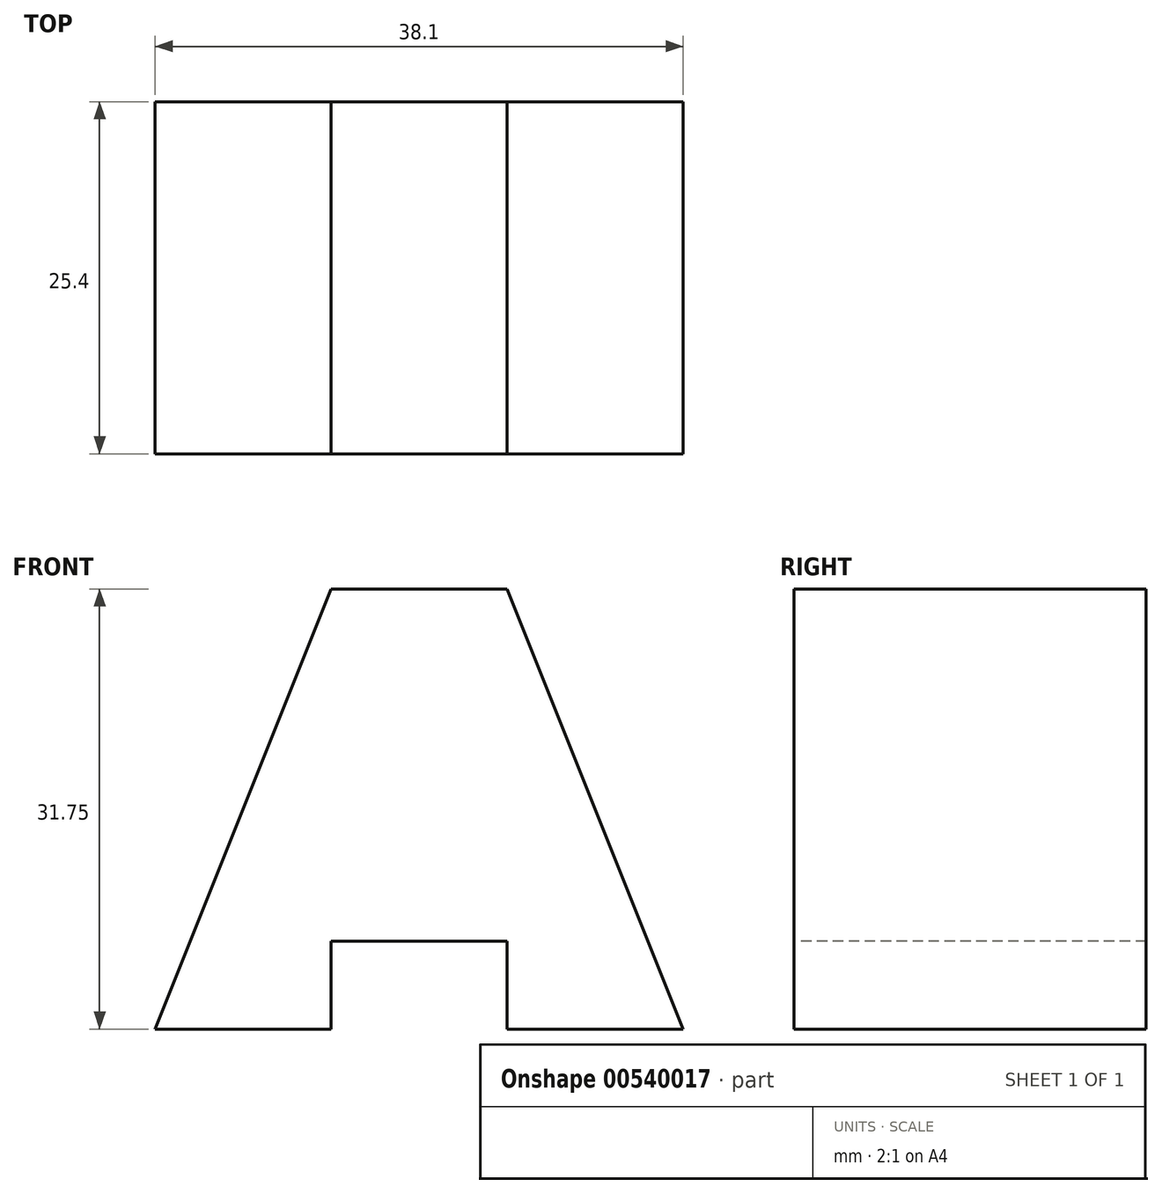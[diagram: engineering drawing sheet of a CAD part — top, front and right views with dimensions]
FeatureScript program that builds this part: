
annotation { "Feature Type Name" : "Feature", "Feature Type Description" : "" }
export const myFeature = defineFeature(function(context is Context, id is Id, definition is map)
    precondition{}
    {
        {
            var Q0;
            Q0=qCreatedBy(makeId("Front.planeOp"),FACE);
            var sketch = newSketch(context, id + "F0", { "sketchPlane" : qUnion([Q0])});
            skLineSegment(sketch, "E0", {"start": v(-62.77, 56) * mm, "end": v(-24.67, 56) * mm});
            skLineSegment(sketch, "E1", {"start": v(-24.67, 56) * mm, "end": v(-24.67, 24.26) * mm});
            skLineSegment(sketch, "E2", {"start": v(-24.67, 24.26) * mm, "end": v(-62.77, 24.26) * mm});
            skLineSegment(sketch, "E3", {"start": v(-62.77, 24.26) * mm, "end": v(-62.77, 56) * mm});
            skSolve(sketch);
        }
        {
            var Q0;
            Q0=makeQuery(id+"F0.imprint","IMPRINT",FACE,{"disambiguationData":[TD([[makeQuery(id+"F0.imprint","IMPRINT",EDGE,{"derivedFrom":sQuery(id+"F0.wireOp",EDGE,"E0")}),-1.0]])]});
            extrude(context, id + "F1", {"entities" : qUnion([Q0]), "depth" : 25.4 * mm, "offsetDistance" : 25.4 * mm});
        }
        {
            var Q0;
            Q0=makeQuery(id+"F1.opExtrude","CAP_FACE",FACE,{"disambiguationData":[OSD([sQuery(id+"F0.wireOp",EDGE,"E0"),sQuery(id+"F0.wireOp",EDGE,"E1"),sQuery(id+"F0.wireOp",EDGE,"E2"),sQuery(id+"F0.wireOp",EDGE,"E3")])],"isStart":false});
            var sketch = newSketch(context, id + "F2", { "sketchPlane" : qUnion([Q0])});
            skLineSegment(sketch, "E4", {"start": v(-50.07, 56) * mm, "end": v(-62.77, 24.26) * mm});
            skLineSegment(sketch, "E5", {"start": v(-37.37, 56) * mm, "end": v(-24.67, 24.26) * mm});
            skSolve(sketch);
        }
        {
            var Q0;
            {var subQ0=sQuery(id+"F2.wireOp",EDGE,"E4");Q0=makeQuery(id+"F2.imprint","IMPRINT",FACE,{"disambiguationData":[TD([[makeQuery(id+"F2.imprint","IMPRINT",EDGE,{"derivedFrom":subQ0}),-1.0]])]});}
            extrude(context, id + "F3", {"entities" : qUnion([Q0]), "operationType" : NewBodyOperationType.REMOVE, "oppositeDirection" : true, "depth" : 25.4 * mm, "offsetDistance" : 25.4 * mm});
        }
        {
            var Q0;
            Q0=makeQuery(id+"F1.opExtrude","CAP_FACE",FACE,{"disambiguationData":[OSD([sQuery(id+"F0.wireOp",EDGE,"E0"),sQuery(id+"F0.wireOp",EDGE,"E1"),sQuery(id+"F0.wireOp",EDGE,"E2"),sQuery(id+"F0.wireOp",EDGE,"E3")])],"isStart":false});
            var sketch = newSketch(context, id + "F4", { "sketchPlane" : qUnion([Q0])});
            skLineSegment(sketch, "E6", {"start": v(-37.37, 56) * mm, "end": v(-24.67, 24.26) * mm});
            skSolve(sketch);
        }
        {
            var Q0;
            {var subQ0=sQuery(id+"F4.wireOp",EDGE,"E6");Q0=makeQuery(id+"F4.imprint","IMPRINT",FACE,{"disambiguationData":[TD([[makeQuery(id+"F4.imprint","IMPRINT",EDGE,{"derivedFrom":subQ0}),1.0]])]});}
            extrude(context, id + "F5", {"entities" : qUnion([Q0]), "operationType" : NewBodyOperationType.REMOVE, "oppositeDirection" : true, "depth" : 25.4 * mm, "offsetDistance" : 25.4 * mm});
        }
        {
            var Q0;
            Q0=makeQuery(id+"F1.opExtrude","CAP_FACE",FACE,{"disambiguationData":[OSD([sQuery(id+"F0.wireOp",EDGE,"E0"),sQuery(id+"F0.wireOp",EDGE,"E1"),sQuery(id+"F0.wireOp",EDGE,"E2"),sQuery(id+"F0.wireOp",EDGE,"E3")])],"isStart":false});
            var sketch = newSketch(context, id + "F6", { "sketchPlane" : qUnion([Q0])});
            skLineSegment(sketch, "E7", {"start": v(-50.07, 24.26) * mm, "end": v(-50.07, 30.6) * mm});
            skLineSegment(sketch, "E8", {"start": v(-50.07, 30.6) * mm, "end": v(-37.37, 30.6) * mm});
            skLineSegment(sketch, "E9", {"start": v(-37.37, 30.6) * mm, "end": v(-37.37, 24.26) * mm});
            skSolve(sketch);
        }
        {
            var Q0;
            {var subQ0=sQuery(id+"F6.wireOp",EDGE,"E7");Q0=makeQuery(id+"F6.imprint","IMPRINT",FACE,{"disambiguationData":[TD([[makeQuery(id+"F6.imprint","IMPRINT",EDGE,{"derivedFrom":subQ0}),-1.0]])]});}
            extrude(context, id + "F7", {"entities" : qUnion([Q0]), "operationType" : NewBodyOperationType.REMOVE, "oppositeDirection" : true, "depth" : 25.4 * mm, "offsetDistance" : 25.4 * mm});
        }
    });
